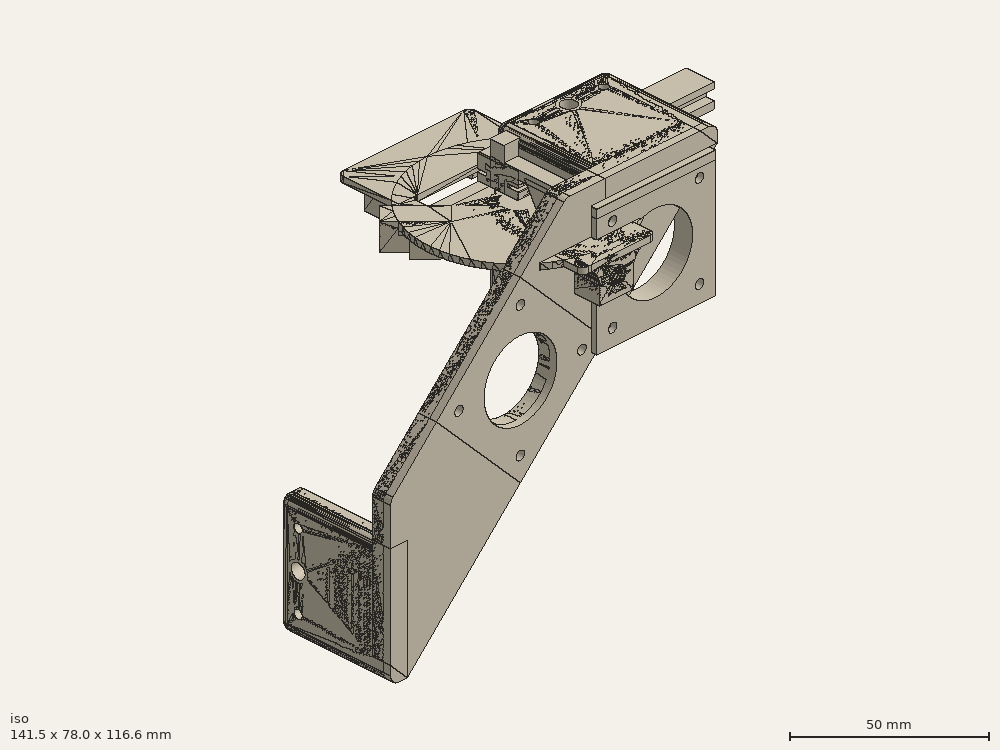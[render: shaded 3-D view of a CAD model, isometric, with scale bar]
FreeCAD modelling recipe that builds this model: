
FCSTD DOCUMENT  (FreeCAD 0.19R)
Label: Gondola
License: All rights reserved
LicenseURL: http://en.wikipedia.org/wiki/All_rights_reserved
objects: Part::Cut×83, Part::Box×63, Part::FeaturePython×39, Part::MultiFuse×29, Part::Cylinder×22, Part::Fillet×20, Part::Prism×2, Part::Fuse×1, Part::Chamfer×1
note: 260 computed .brp shape members not serialized (recipe doc carries the construction recipe); baked Part::Feature solids carry a one-line shape summary decoded from their .brp

FEATURE [Part::Box] Box  label="Cube"
  AttacherType = Attacher::AttachEngine3D
  Height = 10
  Length = 50
  Width = 14.5
FEATURE [Part::Box] Box001  label="Cube001"
  AttacherType = Attacher::AttachEngine3D
  Height = 1
  Length = 50
  Placement = pos=(0,0,4.5) rot=(0,0,1;0rad)
  Width = 4
FEATURE [Part::Box] Box002  label="Cube002"
  AttacherType = Attacher::AttachEngine3D
  Height = 1
  Length = 50
  Placement = pos=(0,11.5,4.5) rot=(0,0,1;0rad)
  Width = 3
FEATURE [Part::Box] Box003  label="Cube003"
  AttacherType = Attacher::AttachEngine3D
  Height = 16
  Length = 10
  Placement = pos=(0,5,0) rot=(0,0,1;0rad)
  Width = 5
FEATURE [Part::Cut] Cut
  Base = -> Box
  Tool = -> Box001
FEATURE [Part::Cut] Cut001
  Base = -> Cut
  Tool = -> Box002
FEATURE [Part::Fuse] Fusion  label="Test_Slider001"
  Base = -> Box003
  Tool = -> Cut001
FEATURE [Part::Box] Box004  label="Cube004"
  AttacherType = Attacher::AttachEngine3D
  Height = 8
  Length = 70
  Width = 10
FEATURE [Part::Box] Box005  label="Cube005"
  AttacherType = Attacher::AttachEngine3D
  Height = 3.5
  Length = 70
  Placement = pos=(0,0,2.5) rot=(0,0,1;0rad)
  Width = 3
FEATURE [Part::Box] Box006  label="Cube006"
  AttacherType = Attacher::AttachEngine3D
  Height = 3.5
  Length = 70
  Placement = pos=(0,7,2.5) rot=(0,0,1;0rad)
  Width = 3
FEATURE [Part::Cut] Cut002
  Base = -> Box004
  Tool = -> Box005
FEATURE [Part::Cut] Cut003  label="Test_Slider002"
  Base = -> Cut002
  Tool = -> Box006
FEATURE [Part::Cylinder] Cylinder
  Angle = 360
  AttacherType = Attacher::AttachEngine3D
  Height = 68
  Placement = pos=(0,5,0) rot=(0,1,0;1.5708rad)
  Radius = 2.5
FEATURE [Part::Cut] Cut004
  Base = -> Cut003
  Tool = -> Cylinder
FEATURE [Part::FeaturePython] Screw  label="M3x30-Screw"  # Fasteners workbench fastener (typed FeaturePython)
  Placement = pos=(20,5,28) rot=(0,0,1;0rad)
  Visibility1 = false
  diameter = 4
  invert = false
  length = 2
  matchOuter = false
  offset = 0
  thread = true
  type = 13
FEATURE [Part::FeaturePython] Screw001  label="M3x30-Screw001"  # Fasteners workbench fastener (typed FeaturePython)
  Placement = pos=(50,5,27) rot=(0,0,1;0rad)
  Visibility1 = false
  diameter = 4
  invert = false
  length = 2
  matchOuter = false
  offset = 0
  thread = true
  type = 13
FEATURE [Part::Cut] Cut005
  Base = -> Cut004
  Tool = -> Screw
FEATURE [Part::Cut] Cut006
  Base = -> Cut005
  Tool = -> Screw001
FEATURE [Part::Box] Box007  label="Cube007"
  AttacherType = Attacher::AttachEngine3D
  Height = 42.3
  Length = 42.3
  Placement = pos=(0,-21,0) rot=(0,0,1;0rad)
  Width = 6.5
FEATURE [Part::Cylinder] Cylinder001
  Angle = 360
  AttacherType = Attacher::AttachEngine3D
  Height = 10
  Placement = pos=(5.65,-14,5.65) rot=(1,0,0;1.5708rad)
  Radius = 1.5
FEATURE [Part::Cylinder] Cylinder002
  Angle = 360
  AttacherType = Attacher::AttachEngine3D
  Height = 10
  Placement = pos=(5.65,-14,36.65) rot=(1,0,0;1.5708rad)
  Radius = 1.5
FEATURE [Part::Cylinder] Cylinder003
  Angle = 360
  AttacherType = Attacher::AttachEngine3D
  Height = 10
  Placement = pos=(36.65,-14,5.65) rot=(1,0,0;1.5708rad)
  Radius = 1.5
FEATURE [Part::Cylinder] Cylinder004
  Angle = 360
  AttacherType = Attacher::AttachEngine3D
  Height = 10
  Placement = pos=(36.65,-14,36.65) rot=(1,0,0;1.5708rad)
  Radius = 1.5
FEATURE [Part::Cut] Cut007
  Base = -> Box007
  Tool = -> Cylinder001
FEATURE [Part::Cut] Cut008
  Base = -> Cut007
  Tool = -> Cylinder004
FEATURE [Part::Cut] Cut009
  Base = -> Cut008
  Tool = -> Cylinder003
FEATURE [Part::Cut] Cut010
  Base = -> Cut009
  Tool = -> Cylinder002
FEATURE [Part::Cylinder] Cylinder005
  Angle = 360
  AttacherType = Attacher::AttachEngine3D
  Height = 10
  Placement = pos=(21.15,-14,21.15) rot=(1,0,0;1.5708rad)
  Radius = 13
FEATURE [Part::Cut] Cut011
  Base = -> Cut010
  Placement = pos=(0,-7,-31.5) rot=(0,0,1;0rad)
  Tool = -> Cylinder005
FEATURE [Part::Box] Box008  label="Cube008"
  AttacherType = Attacher::AttachEngine3D
  Height = 3
  Length = 42.3
  Placement = pos=(0,-28,8) rot=(0,0,1;0rad)
  Width = 38
FEATURE [Part::MultiFuse] Fusion001
  Shapes = -> [Cut011,Box008]
FEATURE [Part::Prism] Prism001
  AttacherType = Attacher::AttachEngine3D
  Circumradius = 23
  FirstAngle = 0
  Height = 2
  Placement = pos=(0,-19,2) rot=(0,1,0;1.5708rad)
  Polygon = 3
  SecondAngle = 0
FEATURE [Part::Box] Box009  label="Cube009"
  AttacherType = Attacher::AttachEngine3D
  Height = 70
  Length = 44
  Placement = pos=(0,-43,-25.5) rot=(0,0,1;0rad)
  Width = 24
FEATURE [Part::Cut] Cut012
  Base = -> Prism001
  Placement = pos=(0,-3,-4) rot=(0,0,1;0rad)
  Tool = -> Box009
FEATURE [Part::Box] Box010  label="Cube010"
  AttacherType = Attacher::AttachEngine3D
  Height = 70
  Length = 44
  Placement = pos=(0,-43,-25.5) rot=(0,0,1;0rad)
  Width = 24
FEATURE [Part::Prism] Prism002
  AttacherType = Attacher::AttachEngine3D
  Circumradius = 23
  FirstAngle = 0
  Height = 2
  Placement = pos=(0,-19,2) rot=(0,1,0;1.5708rad)
  Polygon = 3
  SecondAngle = 0
FEATURE [Part::Cut] Cut013
  Base = -> Prism002
  Placement = pos=(40.3,-3,-4) rot=(0,0,1;0rad)
  Tool = -> Box010
FEATURE [Part::MultiFuse] Fusion002
  Shapes = -> [Fusion001,Cut012]
FEATURE [Part::MultiFuse] Fusion003  label="MotorMountV1"
  Shapes = -> [Cut013,Fusion002]
FEATURE [Part::FeaturePython] ScrewTap  label="M3x27.0-ScrewTap"  # Fasteners workbench fastener (typed FeaturePython)
  Placement = pos=(6,5,10) rot=(0,0,1;0rad)
  Visibility1 = false
  diameter = 4
  invert = false
  length = 27
  matchOuter = false
  offset = 0
  thread = true
FEATURE [Part::Box] Box012  label="Cube012"
  AttacherType = Attacher::AttachEngine3D
  Height = 8
  Length = 70
  Width = 10
FEATURE [Part::Box] Box013  label="Cube013"
  AttacherType = Attacher::AttachEngine3D
  Height = 3.5
  Length = 70
  Placement = pos=(0,0,2.5) rot=(0,0,1;0rad)
  Width = 3
FEATURE [Part::Box] Box014  label="Cube014"
  AttacherType = Attacher::AttachEngine3D
  Height = 3.5
  Length = 70
  Placement = pos=(0,7,2.5) rot=(0,0,1;0rad)
  Width = 3
FEATURE [Part::Cut] Cut014
  Base = -> Box012
  Tool = -> Box013
FEATURE [Part::Cut] Cut015  label="Test_Slider003"
  Base = -> Cut014
  Tool = -> Box014
FEATURE [Part::FeaturePython] Screw002  label="M3x30-Screw002"  # Fasteners workbench fastener (typed FeaturePython)
  Placement = pos=(50,5,27) rot=(0,0,1;0rad)
  Visibility1 = false
  diameter = 4
  invert = false
  length = 2
  matchOuter = false
  offset = 0
  thread = true
  type = 13
FEATURE [Part::Cylinder] Cylinder006
  Angle = 360
  AttacherType = Attacher::AttachEngine3D
  Height = 68
  Placement = pos=(0,5,0) rot=(0,1,0;1.5708rad)
  Radius = 2.5
FEATURE [Part::Cut] Cut017
  Base = -> Cut015
  Tool = -> Cylinder006
FEATURE [Part::FeaturePython] Screw003  label="M3x30-Screw003"  # Fasteners workbench fastener (typed FeaturePython)
  Placement = pos=(20,5,28) rot=(0,0,1;0rad)
  Visibility1 = false
  diameter = 4
  invert = false
  length = 2
  matchOuter = false
  offset = 0
  thread = true
  type = 13
FEATURE [Part::Cut] Cut016
  Base = -> Cut017
  Tool = -> Screw003
FEATURE [Part::Cut] Cut018
  Base = -> Cut016
  Tool = -> Screw002
FEATURE [Part::Box] Box015  label="Cube015"
  AttacherType = Attacher::AttachEngine3D
  Height = 10
  Length = 70
  Placement = pos=(15,0,0) rot=(0,0,1;0rad)
  Width = 10
FEATURE [Part::Cut] Cut019
  Base = -> Cut018
  Tool = -> Box015
FEATURE [Part::Cut] Cut020
  Base = -> Cut019
  Tool = -> ScrewTap
FEATURE [Part::FeaturePython] ScrewTap001  label="(M3.5)x27.0-ScrewTap"  # Fasteners workbench fastener (typed FeaturePython)
  Placement = pos=(12,5,9) rot=(0,0,1;0rad)
  Visibility1 = false
  diameter = 5
  invert = false
  length = 27
  matchOuter = false
  offset = 0
  thread = true
FEATURE [Part::Cut] Cut021
  Base = -> Cut020
  Tool = -> ScrewTap001
FEATURE [Part::Box] Box016  label="Cube016"
  AttacherType = Attacher::AttachEngine3D
  Height = 10.5
  Length = 50
  Width = 14
FEATURE [Part::Box] Box017  label="Cube017"
  AttacherType = Attacher::AttachEngine3D
  Height = 2.3
  Length = 50
  Placement = pos=(0,0,4.1) rot=(0,0,1;0rad)
  Width = 4
FEATURE [Part::Box] Box018  label="Cube018"
  AttacherType = Attacher::AttachEngine3D
  Height = 2.3
  Length = 50
  Placement = pos=(0,10,4.1) rot=(0,0,1;0rad)
  Width = 4
FEATURE [Part::Cut] Cut022
  Base = -> Box016
  Tool = -> Box017
FEATURE [Part::Cut] Cut023
  Base = -> Cut022
  Tool = -> Box018
FEATURE [Part::FeaturePython] ScrewTap002  label="(M3.5)x20.0-ScrewTap"  # Fasteners workbench fastener (typed FeaturePython)
  Placement = pos=(25,7,15) rot=(0,0,1;0rad)
  Visibility1 = false
  diameter = 5
  invert = false
  length = 20
  matchOuter = false
  offset = 0
  thread = true
FEATURE [Part::FeaturePython] ScrewTap003  label="(M3.5)x20.0-ScrewTap003"  # Fasteners workbench fastener (typed FeaturePython)
  Placement = pos=(12.5,7,15) rot=(0,0,1;0rad)
  Visibility1 = false
  diameter = 5
  invert = false
  length = 20
  matchOuter = false
  offset = 0
  thread = true
FEATURE [Part::FeaturePython] ScrewTap004  label="(M3.5)x20.0-ScrewTap002"  # Fasteners workbench fastener (typed FeaturePython)
  Placement = pos=(37.5,7,15) rot=(0,0,1;0rad)
  Visibility1 = false
  diameter = 5
  invert = false
  length = 20
  matchOuter = false
  offset = 0
  thread = true
FEATURE [Part::Cut] Cut024
  Base = -> Cut023
  Tool = -> ScrewTap002
FEATURE [Part::Cut] Cut025
  Base = -> Cut024
  Tool = -> ScrewTap004
FEATURE [Part::Cut] Cut026  label="SliderV4"
  Base = -> Cut025
  Tool = -> ScrewTap003
FEATURE [Part::Box] Box019  label="Cube019"
  AttacherType = Attacher::AttachEngine3D
  Height = 42.3
  Length = 42.3
  Placement = pos=(0,-21,0) rot=(0,0,1;0rad)
  Width = 6.5
FEATURE [Part::Cylinder] Cylinder007
  Angle = 360
  AttacherType = Attacher::AttachEngine3D
  Height = 10
  Placement = pos=(5.65,-14,5.65) rot=(1,0,0;1.5708rad)
  Radius = 1.5
FEATURE [Part::Cylinder] Cylinder008
  Angle = 360
  AttacherType = Attacher::AttachEngine3D
  Height = 10
  Placement = pos=(5.65,-14,36.65) rot=(1,0,0;1.5708rad)
  Radius = 1.5
FEATURE [Part::Cylinder] Cylinder009
  Angle = 360
  AttacherType = Attacher::AttachEngine3D
  Height = 10
  Placement = pos=(36.65,-14,5.65) rot=(1,0,0;1.5708rad)
  Radius = 1.5
FEATURE [Part::Cylinder] Cylinder010
  Angle = 360
  AttacherType = Attacher::AttachEngine3D
  Height = 10
  Placement = pos=(36.65,-14,36.65) rot=(1,0,0;1.5708rad)
  Radius = 1.5
FEATURE [Part::Cut] Cut027
  Base = -> Box019
  Tool = -> Cylinder007
FEATURE [Part::Cut] Cut028
  Base = -> Cut027
  Tool = -> Cylinder010
FEATURE [Part::Cut] Cut029
  Base = -> Cut028
  Tool = -> Cylinder009
FEATURE [Part::Cut] Cut030
  Base = -> Cut029
  Tool = -> Cylinder008
FEATURE [Part::Cylinder] Cylinder011
  Angle = 360
  AttacherType = Attacher::AttachEngine3D
  Height = 10
  Placement = pos=(21.15,-14,21.15) rot=(1,0,0;1.5708rad)
  Radius = 13
FEATURE [Part::Cut] Cut031
  Base = -> Cut030
  Placement = pos=(0,-7,-31.5) rot=(0,0,1;0rad)
  Tool = -> Cylinder011
FEATURE [Part::Box] Box020  label="Cube020"
  AttacherType = Attacher::AttachEngine3D
  Height = 42.3
  Length = 57
  Placement = pos=(42.3,-28,-31.5) rot=(0,0,1;0rad)
  Width = 6.5
FEATURE [Part::Box] Box021  label="Cube021"
  AttacherType = Attacher::AttachEngine3D
  Height = 42.3
  Length = 57
  Placement = pos=(-57,-28,-31.5) rot=(0,0,1;0rad)
  Width = 6.5
FEATURE [Part::MultiFuse] Fusion004
  Shapes = -> [Cut031,Box020]
FEATURE [Part::MultiFuse] Fusion005
  Placement = pos=(-47.5,2,-37) rot=(0,-1,0;0.785398rad)
  Shapes = -> [Fusion004,Box021]
FEATURE [Part::Box] Box022  label="Cube022"
  AttacherType = Attacher::AttachEngine3D
  Height = 6
  Length = 40
  Placement = pos=(5,-26,11) rot=(0,0,1;0rad)
  Width = 40
FEATURE [Part::Box] Box023  label="Cube023"
  AttacherType = Attacher::AttachEngine3D
  Height = 34
  Length = 81
  Placement = pos=(-21,-26,17) rot=(0,0,1;0rad)
  Width = 40
FEATURE [Part::Cut] Cut032
  Base = -> Fusion005
  Tool = -> Box023
FEATURE [Part::FeaturePython] ScrewTap005  label="M6x20.0-ScrewTap"  # Fasteners workbench fastener (typed FeaturePython)
  Placement = pos=(25,7,21) rot=(0,0,1;0rad)
  Visibility1 = false
  diameter = 8
  invert = false
  length = 20
  matchOuter = false
  offset = 0
  thread = false
FEATURE [Part::Cut] Cut033
  Base = -> Box022
  Tool = -> ScrewTap005
FEATURE [Part::FeaturePython] ScrewTap006  label="(M3.5)x20.0-ScrewTap004"  # Fasteners workbench fastener (typed FeaturePython)
  Placement = pos=(12.5,7,22) rot=(0,0,1;0rad)
  Visibility1 = false
  diameter = 5
  invert = false
  length = 20
  matchOuter = false
  offset = 0
  thread = false
FEATURE [Part::FeaturePython] ScrewTap007  label="(M3.5)x20.0-ScrewTap005"  # Fasteners workbench fastener (typed FeaturePython)
  Placement = pos=(37.5,7,22) rot=(0,0,1;0rad)
  Visibility1 = false
  diameter = 5
  invert = false
  length = 20
  matchOuter = false
  offset = 0
  thread = false
FEATURE [Part::Cut] Cut034
  Base = -> Cut033
  Tool = -> ScrewTap006
FEATURE [Part::Cut] Cut035
  Base = -> Cut034
  Tool = -> ScrewTap007
FEATURE [Part::Fillet] Fillet
  Base = -> Cut035
  Edges = 2 edges r=3: [Edge3,Edge14]
FEATURE [Part::Box] Box024  label="Cube024"
  AttacherType = Attacher::AttachEngine3D
  Height = 6
  Length = 40
  Placement = pos=(5,-26,11) rot=(0,0,1;0rad)
  Width = 40
FEATURE [Part::FeaturePython] ScrewTap008  label="M6x20.0-ScrewTap001"  # Fasteners workbench fastener (typed FeaturePython)
  Placement = pos=(25,7,21) rot=(0,0,1;0rad)
  Visibility1 = false
  diameter = 8
  invert = false
  length = 20
  matchOuter = false
  offset = 0
  thread = false
FEATURE [Part::Cut] Cut037
  Base = -> Box024
  Tool = -> ScrewTap008
FEATURE [Part::FeaturePython] ScrewTap009  label="(M3.5)x20.0-ScrewTap006"  # Fasteners workbench fastener (typed FeaturePython)
  Placement = pos=(12.5,7,22) rot=(0,0,1;0rad)
  Visibility1 = false
  diameter = 5
  invert = false
  length = 20
  matchOuter = false
  offset = 0
  thread = false
FEATURE [Part::Cut] Cut036
  Base = -> Cut037
  Tool = -> ScrewTap009
FEATURE [Part::FeaturePython] ScrewTap010  label="(M3.5)x20.0-ScrewTap007"  # Fasteners workbench fastener (typed FeaturePython)
  Placement = pos=(37.5,7,22) rot=(0,0,1;0rad)
  Visibility1 = false
  diameter = 5
  invert = false
  length = 20
  matchOuter = false
  offset = 0
  thread = false
FEATURE [Part::Cut] Cut038
  Base = -> Cut036
  Tool = -> ScrewTap010
FEATURE [Part::Fillet] Fillet001
  Base = -> Cut038
  Edges = 2 edges r=3: [Edge3,Edge14]
  Placement = pos=(-82.5,0,-54.6) rot=(0,1,0;1.5708rad)
FEATURE [Part::Box] Box025  label="Cube025"
  AttacherType = Attacher::AttachEngine3D
  Height = 34
  Length = 81
  Placement = pos=(-105.5,-26,-37.6) rot=(0,1,0;1.5708rad)
  Width = 40
FEATURE [Part::Cut] Cut039
  Base = -> Cut032
  Tool = -> Box025
FEATURE [Part::MultiFuse] Fusion006
  Shapes = -> [Cut039,Fillet001]
FEATURE [Part::MultiFuse] Fusion007
  Shapes = -> [Fusion006,Fillet]
FEATURE [Part::Fillet] Fillet002  label="MotorMountV2"
  Base = -> Fusion007
  Edges = 4 edges r=3: [Edge20,Edge47,Edge84,Edge111]
FEATURE [Part::Box] Box026  label="Cube026"
  AttacherType = Attacher::AttachEngine3D
  Height = 42.3
  Length = 42.3
  Placement = pos=(0,-21,0) rot=(0,0,1;0rad)
  Width = 6.5
FEATURE [Part::Cylinder] Cylinder012
  Angle = 360
  AttacherType = Attacher::AttachEngine3D
  Height = 10
  Placement = pos=(5.65,-14,5.65) rot=(1,0,0;1.5708rad)
  Radius = 1.5
FEATURE [Part::Cylinder] Cylinder013
  Angle = 360
  AttacherType = Attacher::AttachEngine3D
  Height = 10
  Placement = pos=(5.65,-14,36.65) rot=(1,0,0;1.5708rad)
  Radius = 1.5
FEATURE [Part::Cylinder] Cylinder014
  Angle = 360
  AttacherType = Attacher::AttachEngine3D
  Height = 10
  Placement = pos=(36.65,-14,5.65) rot=(1,0,0;1.5708rad)
  Radius = 1.5
FEATURE [Part::Cylinder] Cylinder015
  Angle = 360
  AttacherType = Attacher::AttachEngine3D
  Height = 10
  Placement = pos=(36.65,-14,36.65) rot=(1,0,0;1.5708rad)
  Radius = 1.5
FEATURE [Part::Cut] Cut040
  Base = -> Box026
  Tool = -> Cylinder012
FEATURE [Part::Cut] Cut041
  Base = -> Cut040
  Tool = -> Cylinder015
FEATURE [Part::Cut] Cut042
  Base = -> Cut041
  Tool = -> Cylinder014
FEATURE [Part::Cut] Cut043
  Base = -> Cut042
  Tool = -> Cylinder013
FEATURE [Part::Cylinder] Cylinder016
  Angle = 360
  AttacherType = Attacher::AttachEngine3D
  Height = 10
  Placement = pos=(21.15,-14,21.15) rot=(1,0,0;1.5708rad)
  Radius = 13
FEATURE [Part::Cut] Cut044
  Base = -> Cut043
  Placement = pos=(0,-7,-31.5) rot=(0,0,1;0rad)
  Tool = -> Cylinder016
FEATURE [Part::Box] Box027  label="Cube027"
  AttacherType = Attacher::AttachEngine3D
  Height = 42.3
  Length = 57
  Placement = pos=(42.3,-28,-31.5) rot=(0,0,1;0rad)
  Width = 6.5
FEATURE [Part::Box] Box028  label="Cube028"
  AttacherType = Attacher::AttachEngine3D
  Height = 42.3
  Length = 57
  Placement = pos=(-57,-28,-31.5) rot=(0,0,1;0rad)
  Width = 6.5
FEATURE [Part::MultiFuse] Fusion008
  Shapes = -> [Cut044,Box027]
FEATURE [Part::MultiFuse] Fusion009
  Placement = pos=(-47.5,2,-37) rot=(0,-1,0;0.785398rad)
  Shapes = -> [Fusion008,Box028]
FEATURE [Part::Box] Box029  label="Cube029"
  AttacherType = Attacher::AttachEngine3D
  Height = 6
  Length = 40
  Placement = pos=(5,-26,11) rot=(0,0,1;0rad)
  Width = 40
FEATURE [Part::Box] Box030  label="Cube030"
  AttacherType = Attacher::AttachEngine3D
  Height = 34
  Length = 81
  Placement = pos=(-21,-26,17) rot=(0,0,1;0rad)
  Width = 40
FEATURE [Part::Cut] Cut045
  Base = -> Fusion009
  Tool = -> Box030
FEATURE [Part::FeaturePython] ScrewTap011  label="M8x20.0-ScrewTap"  # Fasteners workbench fastener (typed FeaturePython)
  Placement = pos=(25,7,21) rot=(0,0,1;0rad)
  Visibility1 = false
  diameter = 9
  invert = false
  length = 20
  matchOuter = false
  offset = 0
  thread = false
FEATURE [Part::Cut] Cut046
  Base = -> Box029
  Tool = -> ScrewTap011
FEATURE [Part::FeaturePython] ScrewTap012  label="M4x20.0-ScrewTap001"  # Fasteners workbench fastener (typed FeaturePython)
  Placement = pos=(12.5,7,22) rot=(0,0,1;0rad)
  Visibility1 = false
  diameter = 6
  invert = false
  length = 20
  matchOuter = false
  offset = 0
  thread = false
FEATURE [Part::FeaturePython] ScrewTap013  label="M4x20.0-ScrewTap"  # Fasteners workbench fastener (typed FeaturePython)
  Placement = pos=(37.5,7,22) rot=(0,0,1;0rad)
  Visibility1 = false
  diameter = 6
  invert = false
  length = 20
  matchOuter = false
  offset = 0
  thread = false
FEATURE [Part::Cut] Cut047
  Base = -> Cut046
  Tool = -> ScrewTap012
FEATURE [Part::Cut] Cut048
  Base = -> Cut047
  Tool = -> ScrewTap013
FEATURE [Part::Fillet] Fillet003
  Base = -> Cut048
  Edges = 2 edges r=3: [Edge3,Edge14]
FEATURE [Part::Box] Box031  label="Cube031"
  AttacherType = Attacher::AttachEngine3D
  Height = 6
  Length = 40
  Placement = pos=(5,-26,11) rot=(0,0,1;0rad)
  Width = 40
FEATURE [Part::FeaturePython] ScrewTap014  label="M8x20.0-ScrewTap001"  # Fasteners workbench fastener (typed FeaturePython)
  Placement = pos=(25,7,21) rot=(0,0,1;0rad)
  Visibility1 = false
  diameter = 9
  invert = false
  length = 20
  matchOuter = false
  offset = 0
  thread = false
FEATURE [Part::Cut] Cut050
  Base = -> Box031
  Tool = -> ScrewTap014
FEATURE [Part::FeaturePython] ScrewTap015  label="M4x20.0-ScrewTap003"  # Fasteners workbench fastener (typed FeaturePython)
  Placement = pos=(12.5,7,22) rot=(0,0,1;0rad)
  Visibility1 = false
  diameter = 6
  invert = false
  length = 20
  matchOuter = false
  offset = 0
  thread = false
FEATURE [Part::Cut] Cut049
  Base = -> Cut050
  Tool = -> ScrewTap015
FEATURE [Part::FeaturePython] ScrewTap016  label="M4x20.0-ScrewTap002"  # Fasteners workbench fastener (typed FeaturePython)
  Placement = pos=(37.5,7,22) rot=(0,0,1;0rad)
  Visibility1 = false
  diameter = 6
  invert = false
  length = 20
  matchOuter = false
  offset = 0
  thread = false
FEATURE [Part::Cut] Cut051
  Base = -> Cut049
  Tool = -> ScrewTap016
FEATURE [Part::Fillet] Fillet004
  Base = -> Cut051
  Edges = 2 edges r=3: [Edge3,Edge14]
  Placement = pos=(-82.5,0,-54.6) rot=(0,1,0;1.5708rad)
FEATURE [Part::Box] Box032  label="Cube032"
  AttacherType = Attacher::AttachEngine3D
  Height = 34
  Length = 81
  Placement = pos=(-105.5,-26,-37.6) rot=(0,1,0;1.5708rad)
  Width = 40
FEATURE [Part::Cut] Cut052
  Base = -> Cut045
  Tool = -> Box032
FEATURE [Part::MultiFuse] Fusion010
  Shapes = -> [Cut052,Fillet004]
FEATURE [Part::MultiFuse] Fusion011
  Shapes = -> [Fusion010,Fillet003]
FEATURE [Part::Fillet] Fillet005  label="MotorMountV003"
  Base = -> Fusion011
  Edges = 4 edges r=3: [Edge20,Edge47,Edge84,Edge111]
FEATURE [Part::Box] Box033  label="Cube033"
  AttacherType = Attacher::AttachEngine3D
  Height = 10
  Length = 100
  Placement = pos=(-35,-19,3.5) rot=(0,0,1;0rad)
  Width = 100
FEATURE [Part::Box] Box034  label="Cube034"
  AttacherType = Attacher::AttachEngine3D
  Height = 100
  Length = 10
  Placement = pos=(-67,-19,-112.5) rot=(0,0,1;0rad)
  Width = 100
FEATURE [Part::Box] Box036  label="Cube036"
  AttacherType = Attacher::AttachEngine3D
  Height = 210
  Length = 210
  Placement = pos=(-77,-223.5,-108) rot=(0,0,1;0rad)
  Width = 200
FEATURE [Part::Cut] Cut053
  Base = -> Fillet005
  Tool = -> Box033
FEATURE [Part::Cut] Cut054
  Base = -> Cut053
  Tool = -> Box036
FEATURE [Part::Cut] Cut055  label="MotorMountV3"
  Base = -> Cut054
  Tool = -> Box034
FEATURE [Part::FeaturePython] Tube  # WARN: FeaturePython — macro-defined, semantics opaque (R4)
  AttacherType = Attacher::AttachEngine3D
  Height = 30
  InnerRadius = 5
  OuterRadius = 7
  Visibility1 = false
FEATURE [Part::FeaturePython] ScrewTap017  label="(M3.5)x20.0-ScrewTap011"  # Fasteners workbench fastener (typed FeaturePython)
  Placement = pos=(0,0,7) rot=(1,0,0;1.5708rad)
  Visibility1 = false
  diameter = 5
  invert = false
  length = 20
  matchOuter = false
  offset = 0
  thread = true
FEATURE [Part::Cut] Cut056
  Base = -> Tube
  Placement = pos=(0,0,-29) rot=(0,0,1;0rad)
  Tool = -> ScrewTap017
FEATURE [Part::Cylinder] Cylinder018
  Angle = 360
  AttacherType = Attacher::AttachEngine3D
  Height = 2
  Radius = 32
FEATURE [Part::Cylinder] Cylinder019
  Angle = 360
  AttacherType = Attacher::AttachEngine3D
  Height = 15
  Placement = pos=(0,0,-3) rot=(0,0,1;0rad)
  Radius = 5
FEATURE [Part::Cut] Cut057
  Base = -> Cylinder018
  Tool = -> Cylinder019
FEATURE [Part::Box] Box037  label="Cube037"
  AttacherType = Attacher::AttachEngine3D
  Height = 12
  Length = 12
  Placement = pos=(-6,-27,-12) rot=(0,0,1;0rad)
  Width = 12
FEATURE [Part::FeaturePython] ScrewTap018  label="M6x20.0-ScrewTap002"  # Fasteners workbench fastener (typed FeaturePython)
  Placement = pos=(0,-14,-6) rot=(-1,0,0;1.5708rad)
  Visibility1 = false
  diameter = 8
  invert = false
  length = 20
  matchOuter = false
  offset = 0
  thread = true
FEATURE [Part::Cut] Cut058
  Base = -> Box037
  Placement = pos=(0,-8,0) rot=(0,0,1;0rad)
  Tool = -> ScrewTap018
FEATURE [Part::Box] Box039  label="Cube039"
  AttacherType = Attacher::AttachEngine3D
  Height = 10
  Length = 36
  Placement = pos=(-18,14,0) rot=(0,0,1;0rad)
  Width = 6
FEATURE [Part::Box] Box040  label="Cube040"
  AttacherType = Attacher::AttachEngine3D
  Height = 2
  Length = 26
  Placement = pos=(-13,-36,0) rot=(0,0,1;0rad)
  Width = 16
FEATURE [Part::MultiFuse] Fusion012
  Shapes = -> [Cut058,Box040]
FEATURE [Part::Fillet] Fillet006
  Base = -> Fusion012
  Edges = 2 edges r=6: [Edge13,Edge15]
FEATURE [Part::MultiFuse] Fusion013
  Shapes = -> [Cut057,Fillet006]
FEATURE [Part::Fillet] Fillet007
  Base = -> Fusion013
  Edges = 2 edges r=3: [Edge14,Edge21]
FEATURE [Part::Fillet] Fillet008
  Base = -> Fillet007
  Edges = 2 edges r=1.5: [Edge64,Edge65]
FEATURE [Part::Box] Box041  label="Cube041"
  AttacherType = Attacher::AttachEngine3D
  Height = 2
  Length = 47
  Placement = pos=(-22.5,20,0) rot=(0,0,1;0rad)
  Width = 22
FEATURE [Part::Box] Box042  label="Cube042"
  AttacherType = Attacher::AttachEngine3D
  Height = 12
  Length = 7
  Placement = pos=(16.5,33,-12) rot=(0,0,1;0rad)
  Width = 8
FEATURE [Part::Box] Box043  label="Cube043"
  AttacherType = Attacher::AttachEngine3D
  Height = 12
  Length = 7
  Placement = pos=(-14,33,-12) rot=(0,0,1;0rad)
  Width = 8
FEATURE [Part::MultiFuse] Fusion014
  Shapes = -> [Box041,Box042,Box043]
FEATURE [Part::MultiFuse] Fusion015
  Shapes = -> [Fusion014,Fillet008]
FEATURE [Part::Cut] Cut059
  Base = -> Fusion015
  Tool = -> Box039
FEATURE [Part::Cylinder] Cylinder020
  Angle = 360
  AttacherType = Attacher::AttachEngine3D
  Height = 33
  Placement = pos=(0,0,0) rot=(1,0,0;1.5708rad)
  Radius = 2
FEATURE [Part::Chamfer] Chamfer
  Base = -> Cylinder020
  Edges = 1 edges r=1: [Edge3]
  Placement = pos=(0,0,0) rot=(0,0,1;2.35619rad)
FEATURE [Part::Box] Box044  label="Cube044"
  AttacherType = Attacher::AttachEngine3D
  Height = 9
  Length = 8
  Placement = pos=(18,23,-7) rot=(0,0,1;0rad)
  Width = 18
FEATURE [Part::Box] Box045  label="Cube045"
  AttacherType = Attacher::AttachEngine3D
  Height = 7
  Length = 2
  Placement = pos=(21,20.5,-7) rot=(0,0,-1;0rad)
  Width = 25
FEATURE [Part::Cut] Cut060
  Base = -> Box044
  Placement = pos=(-13,18,0) rot=(0,0,-1;0rad)
  Tool = -> Box045
FEATURE [Part::FeaturePython] ScrewTap019  label="M2x20.0-ScrewTap003"  # Fasteners workbench fastener (typed FeaturePython)
  Placement = pos=(14,47,-3) rot=(0,1,0;1.5708rad)
  Visibility1 = false
  diameter = 2
  invert = false
  length = 20
  matchOuter = false
  offset = 0
  thread = true
FEATURE [Part::MultiFuse] Fusion016
  Shapes = -> [Cut059,Cut056]
FEATURE [Part::Cut] Cut061
  Base = -> Cut060
  Placement = pos=(-19,-15,0) rot=(0,0,-1;0.785398rad)
  Tool = -> ScrewTap019
FEATURE [Part::Box] Box046  label="Cube046"
  AttacherType = Attacher::AttachEngine3D
  Height = 9
  Length = 8
  Placement = pos=(18,23,-7) rot=(0,0,1;0rad)
  Width = 18
FEATURE [Part::Box] Box047  label="Cube047"
  AttacherType = Attacher::AttachEngine3D
  Height = 7
  Length = 2
  Placement = pos=(21,20.5,-7) rot=(0,0,-1;0rad)
  Width = 25
FEATURE [Part::Cut] Cut062
  Base = -> Box046
  Placement = pos=(-13,18,0) rot=(0,0,-1;0rad)
  Tool = -> Box047
FEATURE [Part::FeaturePython] ScrewTap020  label="M2x20.0-ScrewTap002"  # Fasteners workbench fastener (typed FeaturePython)
  Placement = pos=(14,47,-3) rot=(0,1,0;1.5708rad)
  Visibility1 = false
  diameter = 2
  invert = false
  length = 20
  matchOuter = false
  offset = 0
  thread = true
FEATURE [Part::Cut] Cut063
  Base = -> Cut062
  Placement = pos=(6,-28,0) rot=(0,0,1;0.785398rad)
  Tool = -> ScrewTap020
FEATURE [Part::MultiFuse] Fusion017
  Shapes = -> [Cut061,Cut063]
FEATURE [Part::MultiFuse] Fusion018
  Shapes = -> [Fusion016,Fusion017]
FEATURE [Part::FeaturePython] ScrewTap021  label="M2x20.0-ScrewTap"  # Fasteners workbench fastener (typed FeaturePython)
  Placement = pos=(19,18,-6) rot=(1,0,0;1.5708rad)
  Visibility1 = false
  diameter = 2
  invert = false
  length = 20
  matchOuter = false
  offset = 0
  thread = true
FEATURE [Part::FeaturePython] ScrewTap022  label="M2x20.0-ScrewTap001"  # Fasteners workbench fastener (typed FeaturePython)
  Placement = pos=(-9.5,17,-6) rot=(1,0,0;1.5708rad)
  Visibility1 = false
  diameter = 2
  invert = false
  length = 20
  matchOuter = false
  offset = 0
  thread = true
FEATURE [Part::Cut] Cut064
  Base = -> Fusion018
  Tool = -> ScrewTap021
FEATURE [Part::Cut] Cut065
  Base = -> Cut064
  Tool = -> ScrewTap022
FEATURE [Part::Fillet] Fillet009  label="GondolaV1"
  Base = -> Cut065
  Edges = 4 edges r=2: [Edge19,Edge20,Edge33,Edge36]
FEATURE [Part::Box] Box048  label="Cube048"
  AttacherType = Attacher::AttachEngine3D
  Height = 7
  Length = 4
  Placement = pos=(-23.5,4,-7) rot=(0,0,1;0.785398rad)
  Width = 8
FEATURE [Part::FeaturePython] ScrewTap023  label="(M3.5)x20.0-ScrewTap012"  # Fasteners workbench fastener (typed FeaturePython)
  Placement = pos=(0,0,0) rot=(1,0,0;1.5708rad)
  Visibility1 = false
  diameter = 5
  invert = false
  length = 20
  matchOuter = false
  offset = 0
  thread = true
FEATURE [Part::Box] Box049  label="Cube049"
  AttacherType = Attacher::AttachEngine3D
  Height = 7
  Length = 8
  Placement = pos=(-4,0,-4) rot=(0,0,1;0rad)
  Width = 8
FEATURE [Part::Cut] Cut066
  Base = -> ScrewTap023
  Placement = pos=(-32.5,0.5,-3) rot=(0,0,-1;0.785398rad)
  Tool = -> Box049
FEATURE [Part::Box] Box050  label="Cube050"
  AttacherType = Attacher::AttachEngine3D
  Height = 7
  Length = 3.5
  Placement = pos=(20,6,-7) rot=(0,0,-1;0.785398rad)
  Width = 8
FEATURE [Part::Box] Box051  label="Cube051"
  AttacherType = Attacher::AttachEngine3D
  Height = 7
  Length = 8
  Placement = pos=(-4,0,-4) rot=(0,0,1;0rad)
  Width = 8
FEATURE [Part::FeaturePython] ScrewTap024  label="(M3.5)x20.0-ScrewTap013"  # Fasteners workbench fastener (typed FeaturePython)
  Placement = pos=(0,0,0) rot=(1,0,0;1.5708rad)
  Visibility1 = false
  diameter = 5
  invert = false
  length = 20
  matchOuter = false
  offset = 0
  thread = true
FEATURE [Part::Cut] Cut067
  Base = -> ScrewTap024
  Placement = pos=(31.5,0.5,-3) rot=(0,0,1;0.785398rad)
  Tool = -> Box051
FEATURE [Part::FeaturePython] Tube001  # WARN: FeaturePython — macro-defined, semantics opaque (R4)
  AttacherType = Attacher::AttachEngine3D
  Height = 30
  InnerRadius = 5.5
  OuterRadius = 7
  Visibility1 = false
FEATURE [Part::FeaturePython] ScrewTap025  label="(M3.5)x20.0-ScrewTap014"  # Fasteners workbench fastener (typed FeaturePython)
  Placement = pos=(0,0,7) rot=(1,0,0;1.5708rad)
  Visibility1 = false
  diameter = 5
  invert = false
  length = 20
  matchOuter = false
  offset = 0
  thread = true
FEATURE [Part::Cut] Cut068
  Base = -> Tube001
  Placement = pos=(0,0,-29) rot=(0,0,1;0rad)
  Tool = -> ScrewTap025
FEATURE [Part::Cylinder] Cylinder021
  Angle = 360
  AttacherType = Attacher::AttachEngine3D
  Height = 2
  Radius = 32
FEATURE [Part::Cylinder] Cylinder022
  Angle = 360
  AttacherType = Attacher::AttachEngine3D
  Height = 15
  Placement = pos=(0,0,-3) rot=(0,0,1;0rad)
  Radius = 5
FEATURE [Part::Cut] Cut069
  Base = -> Cylinder021
  Tool = -> Cylinder022
FEATURE [Part::Box] Box052  label="Cube052"
  AttacherType = Attacher::AttachEngine3D
  Height = 12
  Length = 12
  Placement = pos=(-6,-27,-12) rot=(0,0,1;0rad)
  Width = 12
FEATURE [Part::FeaturePython] ScrewTap026  label="M8x20.0-ScrewTap002"  # Fasteners workbench fastener (typed FeaturePython)
  Placement = pos=(0,-14,-6) rot=(-1,0,0;1.5708rad)
  Visibility1 = false
  diameter = 9
  invert = false
  length = 20
  matchOuter = false
  offset = 0
  thread = true
FEATURE [Part::Cut] Cut070
  Base = -> Box052
  Placement = pos=(0,-8,0) rot=(0,0,1;0rad)
  Tool = -> ScrewTap026
FEATURE [Part::Box] Box053  label="Cube053"
  AttacherType = Attacher::AttachEngine3D
  Height = 10
  Length = 36
  Placement = pos=(-18,14,0) rot=(0,0,1;0rad)
  Width = 6
FEATURE [Part::Box] Box054  label="Cube054"
  AttacherType = Attacher::AttachEngine3D
  Height = 2
  Length = 26
  Placement = pos=(-13,-36,0) rot=(0,0,1;0rad)
  Width = 16
FEATURE [Part::MultiFuse] Fusion019
  Shapes = -> [Cut070,Box054]
FEATURE [Part::Fillet] Fillet010
  Base = -> Fusion019
  Edges = 2 edges r=6: [Edge13,Edge15]
FEATURE [Part::MultiFuse] Fusion020
  Shapes = -> [Cut069,Fillet010]
FEATURE [Part::Fillet] Fillet011
  Base = -> Fusion020
  Edges = 2 edges r=3: [Edge14,Edge21]
FEATURE [Part::Fillet] Fillet012
  Base = -> Fillet011
  Edges = 3 edges r=0.2: [Edge17,Edge18,Edge19]
FEATURE [Part::Box] Box055  label="Cube055"
  AttacherType = Attacher::AttachEngine3D
  Height = 2
  Length = 47
  Placement = pos=(-22.5,20,0) rot=(0,0,1;0rad)
  Width = 22
FEATURE [Part::Box] Box056  label="Cube056"
  AttacherType = Attacher::AttachEngine3D
  Height = 12
  Length = 7
  Placement = pos=(16.5,33,-12) rot=(0,0,1;0rad)
  Width = 8
FEATURE [Part::Box] Box057  label="Cube057"
  AttacherType = Attacher::AttachEngine3D
  Height = 12
  Length = 7
  Placement = pos=(-14,33,-12) rot=(0,0,1;0rad)
  Width = 8
FEATURE [Part::MultiFuse] Fusion021
  Shapes = -> [Box055,Box056,Box057]
FEATURE [Part::MultiFuse] Fusion022
  Shapes = -> [Fusion021,Fillet012]
FEATURE [Part::Cut] Cut071
  Base = -> Fusion022
  Tool = -> Box053
FEATURE [Part::Box] Box058  label="Cube058"
  AttacherType = Attacher::AttachEngine3D
  Height = 9
  Length = 8
  Placement = pos=(18,23,-7) rot=(0,0,1;0rad)
  Width = 18
FEATURE [Part::Box] Box059  label="Cube059"
  AttacherType = Attacher::AttachEngine3D
  Height = 7
  Length = 2
  Placement = pos=(21,20.5,-7) rot=(0,0,-1;0rad)
  Width = 25
FEATURE [Part::Cut] Cut072
  Base = -> Box058
  Placement = pos=(-13,18,0) rot=(0,0,-1;0rad)
  Tool = -> Box059
FEATURE [Part::FeaturePython] ScrewTap027  label="M2x20.0-ScrewTap004"  # Fasteners workbench fastener (typed FeaturePython)
  Placement = pos=(14,47,-3) rot=(0,1,0;1.5708rad)
  Visibility1 = false
  diameter = 2
  invert = false
  length = 20
  matchOuter = false
  offset = 0
  thread = true
FEATURE [Part::MultiFuse] Fusion023
  Shapes = -> [Cut071,Cut068]
FEATURE [Part::Cut] Cut073
  Base = -> Cut072
  Placement = pos=(-19,-15,0) rot=(0,0,-1;0.785398rad)
  Tool = -> ScrewTap027
FEATURE [Part::Box] Box060  label="Cube060"
  AttacherType = Attacher::AttachEngine3D
  Height = 9
  Length = 8
  Placement = pos=(18,23,-7) rot=(0,0,1;0rad)
  Width = 18
FEATURE [Part::Box] Box061  label="Cube061"
  AttacherType = Attacher::AttachEngine3D
  Height = 7
  Length = 2
  Placement = pos=(21,20.5,-7) rot=(0,0,-1;0rad)
  Width = 25
FEATURE [Part::Cut] Cut074
  Base = -> Box060
  Placement = pos=(-13,18,0) rot=(0,0,-1;0rad)
  Tool = -> Box061
FEATURE [Part::FeaturePython] ScrewTap028  label="M2x20.0-ScrewTap005"  # Fasteners workbench fastener (typed FeaturePython)
  Placement = pos=(14,47,-3) rot=(0,1,0;1.5708rad)
  Visibility1 = false
  diameter = 2
  invert = false
  length = 20
  matchOuter = false
  offset = 0
  thread = true
FEATURE [Part::Cut] Cut075
  Base = -> Cut074
  Placement = pos=(6,-28,0) rot=(0,0,1;0.785398rad)
  Tool = -> ScrewTap028
FEATURE [Part::MultiFuse] Fusion024
  Shapes = -> [Cut073,Cut075]
FEATURE [Part::MultiFuse] Fusion025
  Shapes = -> [Fusion023,Fusion024]
FEATURE [Part::FeaturePython] ScrewTap029  label="M2x20.0-ScrewTap006"  # Fasteners workbench fastener (typed FeaturePython)
  Placement = pos=(19,18,-6) rot=(1,0,0;1.5708rad)
  Visibility1 = false
  diameter = 2
  invert = false
  length = 20
  matchOuter = false
  offset = 0
  thread = true
FEATURE [Part::FeaturePython] ScrewTap030  label="M2x20.0-ScrewTap007"  # Fasteners workbench fastener (typed FeaturePython)
  Placement = pos=(-9.5,17,-6) rot=(1,0,0;1.5708rad)
  Visibility1 = false
  diameter = 2
  invert = false
  length = 20
  matchOuter = false
  offset = 0
  thread = true
FEATURE [Part::Cut] Cut076
  Base = -> Fusion025
  Tool = -> ScrewTap029
FEATURE [Part::Cut] Cut077
  Base = -> Cut076
  Tool = -> ScrewTap030
FEATURE [Part::Fillet] Fillet013  label="GondolaV002"
  Base = -> Cut077
  Edges = 4 edges r=2: [Edge19,Edge20,Edge33,Edge36]
FEATURE [Part::MultiFuse] Fusion026
  Shapes = -> [Fillet013,Box050]
FEATURE [Part::MultiFuse] Fusion027
  Shapes = -> [Fusion026,Box048]
FEATURE [Part::Cut] Cut078
  Base = -> Fusion027
  Tool = -> Cut067
FEATURE [Part::Cut] Cut079
  Base = -> Cut078
  Tool = -> Cut066
FEATURE [Part::Fillet] Fillet014
  Base = -> Cut079
  Edges = 6 edges r=2: [Edge2,Edge17,Edge19,Edge29,Edge31,Edge33]
FEATURE [Part::Fillet] Fillet015  label="GondolaV2"
  Base = -> Fillet014
  Edges = 5 edges r=1.1: [Edge63,Edge65,Edge150,Edge169,Edge170]
FEATURE [Part::Box] Box062  label="Cube062"
  AttacherType = Attacher::AttachEngine3D
  Height = 12
  Length = 12
  Placement = pos=(-6,-27,-12) rot=(0,0,1;0rad)
  Width = 12
FEATURE [Part::FeaturePython] ScrewTap031  label="M6x20.0-ScrewTap004"  # Fasteners workbench fastener (typed FeaturePython)
  Placement = pos=(0,-14,-6) rot=(-1,0,0;1.5708rad)
  Visibility1 = false
  diameter = 8
  invert = false
  length = 20
  matchOuter = false
  offset = 0
  thread = true
FEATURE [Part::Cut] Cut080
  Base = -> Box062
  Placement = pos=(0,-8,0) rot=(0,0,1;0rad)
  Tool = -> ScrewTap031
FEATURE [Part::Box] Box063  label="Cube063"
  AttacherType = Attacher::AttachEngine3D
  Height = 2
  Length = 26
  Placement = pos=(-13,-36,0) rot=(0,0,1;0rad)
  Width = 44
FEATURE [Part::MultiFuse] Fusion028
  Shapes = -> [Cut080,Box063]
FEATURE [Part::Fillet] Fillet016
  Base = -> Fusion028
  Edges = 2 edges r=6: [Edge13,Edge15]
FEATURE [Part::Box] Box064  label="Cube064"
  AttacherType = Attacher::AttachEngine3D
  Height = 9
  Length = 12
  Placement = pos=(16,23,-7) rot=(0,0,1;0rad)
  Width = 18
FEATURE [Part::Box] Box065  label="Cube065"
  AttacherType = Attacher::AttachEngine3D
  Height = 7
  Length = 2
  Placement = pos=(21,20.5,-7) rot=(0,0,-1;0rad)
  Width = 25
FEATURE [Part::Cut] Cut081
  Base = -> Box064
  Placement = pos=(-22,-33,-2) rot=(0,0,-1;0rad)
  Tool = -> Box065
FEATURE [Part::MultiFuse] Fusion029
  Shapes = -> [Cut081,Fillet016]
FEATURE [Part::FeaturePython] ScrewTap032  label="(M3.5)x20.0-ScrewTap015"  # Fasteners workbench fastener (typed FeaturePython)
  Placement = pos=(9,-2,-5) rot=(0,1,0;1.5708rad)
  Visibility1 = false
  diameter = 5
  invert = false
  length = 20
  matchOuter = false
  offset = 0
  thread = true
FEATURE [Part::Cut] Cut082
  Base = -> Fusion029
  Tool = -> ScrewTap032
FEATURE [Part::Fillet] Fillet017
  Base = -> Cut082
  Edges = 2 edges r=3.5: [Edge2,Edge4]
FEATURE [Part::Fillet] Fillet018
  Base = -> Fillet017
  Edges = 2 edges r=3.5: [Edge19,Edge21]
FEATURE [Part::Fillet] Fillet019  label="WeightV1"
  Base = -> Fillet018
  Edges = 2 edges r=2: [Edge20,Edge24]
